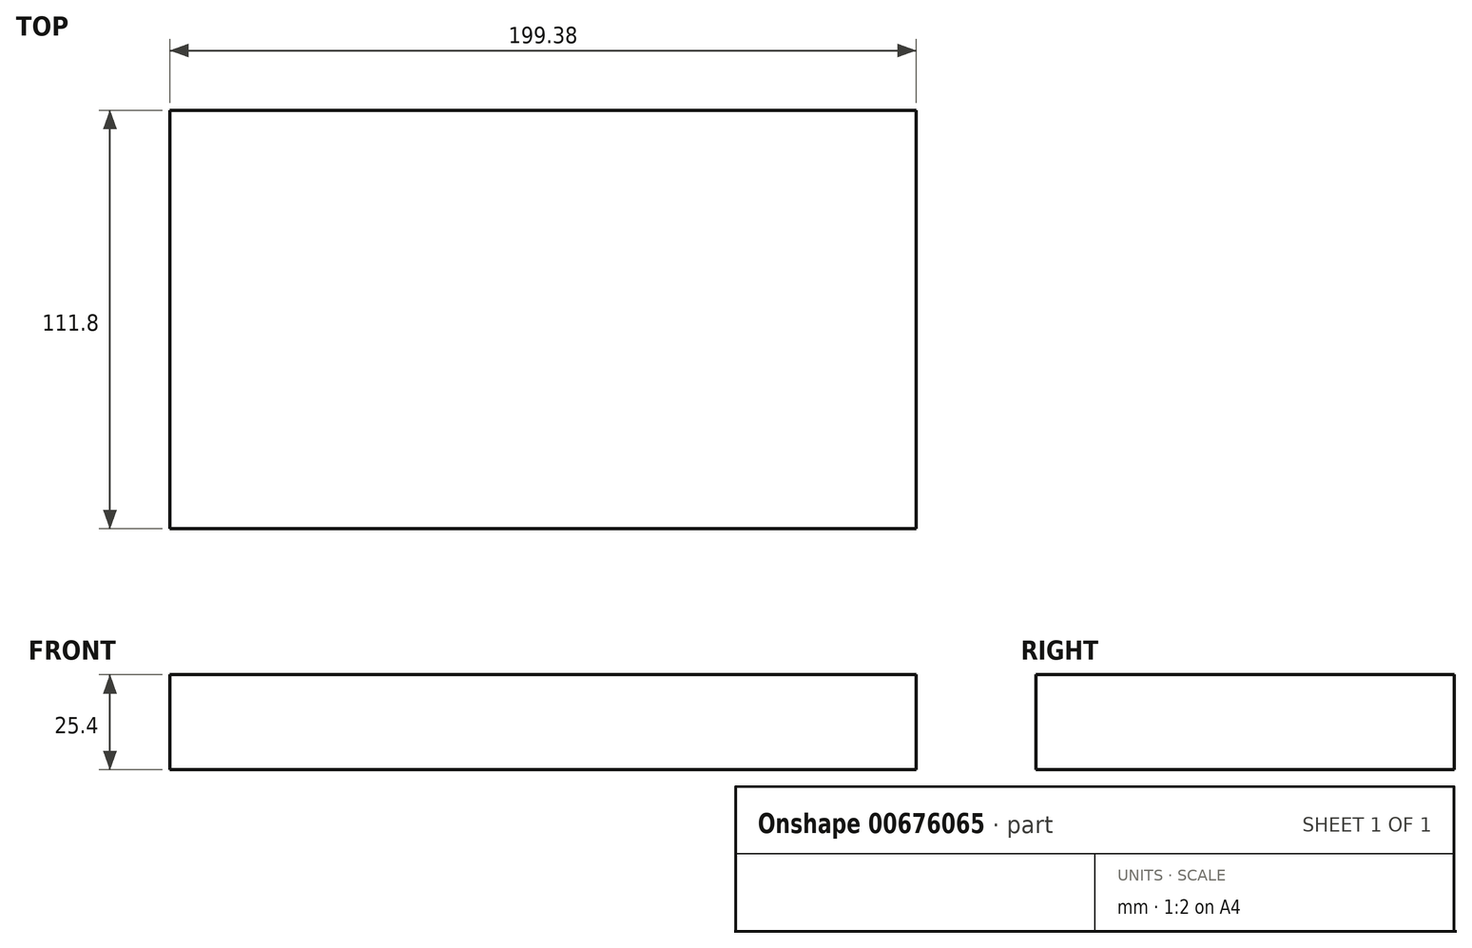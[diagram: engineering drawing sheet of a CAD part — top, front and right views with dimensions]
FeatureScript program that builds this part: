
annotation { "Feature Type Name" : "Feature", "Feature Type Description" : "" }
export const myFeature = defineFeature(function(context is Context, id is Id, definition is map)
    precondition{}
    {
        {
            var Q0;
            Q0=qCreatedBy(makeId("Top.planeOp"),FACE);
            var sketch = newSketch(context, id + "F0", { "sketchPlane" : qUnion([Q0])});
            skLineSegment(sketch, "E0.bottom", {"start": v(-99.58, 56.12) * mm, "end": v(99.8, 56.12) * mm});
            skLineSegment(sketch, "E0.top", {"start": v(-99.58, -55.68) * mm, "end": v(99.8, -55.68) * mm});
            skLineSegment(sketch, "E0.left", {"start": v(-99.58, 56.12) * mm, "end": v(-99.58, -55.68) * mm});
            skLineSegment(sketch, "E0.right", {"start": v(99.8, 56.12) * mm, "end": v(99.8, -55.68) * mm});
            skSolve(sketch);
        }
        {
            var Q0;
            Q0 = qSketchRegion(id + "F0", true);
            extrude(context, id + "F1", {"entities" : qUnion([Q0]), "depth" : 25.4 * mm, "offsetDistance" : 25.4 * mm});
        }
    });
